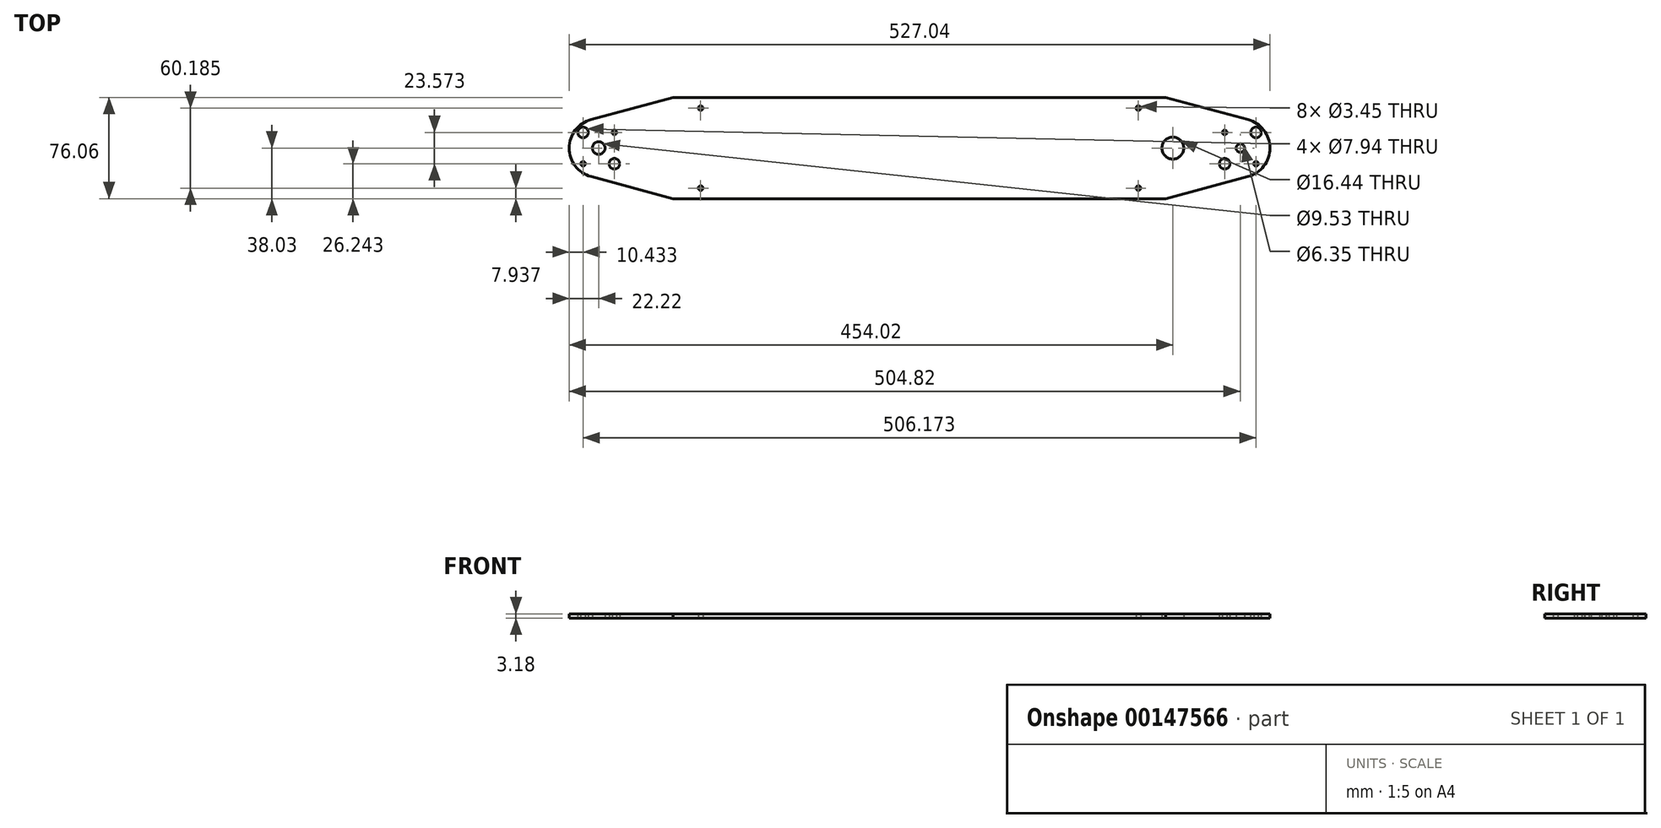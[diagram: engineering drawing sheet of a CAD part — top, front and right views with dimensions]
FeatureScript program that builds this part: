
annotation { "Feature Type Name" : "Feature", "Feature Type Description" : "" }
export const myFeature = defineFeature(function(context is Context, id is Id, definition is map)
    precondition{}
    {
        {
            var Q0;
            Q0=qCreatedBy(makeId("Top.planeOp"),FACE);
            var sketch = newSketch(context, id + "F0", { "sketchPlane" : qUnion([Q0])});
            skPoint(sketch, "E0.rect.middle", {"position": v(0, 0) * mm});
            skCircle(sketch, "E1", {"center": v(0, 0) * mm, "radius": 11.11 * mm, "construction": true});
            skLineSegment(sketch, "E2.bottom", {"start": v(11.79, 11.79) * mm, "end": v(-11.79, 11.79) * mm, "construction": true});
            skLineSegment(sketch, "E2.left", {"start": v(11.79, 11.79) * mm, "end": v(11.79, -11.79) * mm, "construction": true});
            skLineSegment(sketch, "E2.right", {"start": v(-11.79, 11.79) * mm, "end": v(-11.79, -11.79) * mm, "construction": true});
            skCircle(sketch, "E3", {"center": v(11.79, 11.79) * mm, "radius": 5.56 * mm, "construction": true});
            skCircle(sketch, "E4", {"center": v(-11.79, 11.79) * mm, "radius": 1.73 * mm});
            skCircle(sketch, "E5", {"center": v(11.79, 11.79) * mm, "radius": 3.97 * mm});
            skCircle(sketch, "E6", {"center": v(11.79, -11.79) * mm, "radius": 1.73 * mm});
            skCircle(sketch, "E7", {"center": v(-11.79, -11.79) * mm, "radius": 3.97 * mm});
            skArc(sketch, "E8", {"start": v(-488.35, 21.47) * mm, "mid": v(-504.83, 0) * mm, "end": v(-488.35, -21.47) * mm});
            skLineSegment(sketch, "E9.bottom", {"start": v(-494.39, 11.79) * mm, "end": v(-470.81, 11.79) * mm, "construction": true});
            skLineSegment(sketch, "E9.top", {"start": v(-494.39, -11.79) * mm, "end": v(-470.81, -11.79) * mm, "construction": true});
            skLineSegment(sketch, "E9.left", {"start": v(-494.39, 11.79) * mm, "end": v(-494.39, -11.79) * mm, "construction": true});
            skLineSegment(sketch, "E9.right", {"start": v(-470.81, 11.79) * mm, "end": v(-470.81, -11.79) * mm, "construction": true});
            skCircle(sketch, "E10", {"center": v(-470.81, 11.79) * mm, "radius": 1.73 * mm});
            skCircle(sketch, "E11", {"center": v(-482.6, 0) * mm, "radius": 4.76 * mm});
            skCircle(sketch, "E12", {"center": v(-494.39, 11.79) * mm, "radius": 3.97 * mm});
            skCircle(sketch, "E13", {"center": v(-494.39, -11.79) * mm, "radius": 1.73 * mm});
            skCircle(sketch, "E14", {"center": v(-470.81, -11.79) * mm, "radius": 3.97 * mm});
            skLineSegment(sketch, "E15", {"start": v(0, 0) * mm, "end": v(-482.6, 0) * mm, "construction": true});
            skLineSegment(sketch, "E16", {"start": v(-488.35, -21.47) * mm, "end": v(-426.54, -38.03) * mm});
            skLineSegment(sketch, "E17", {"start": v(-488.35, 21.47) * mm, "end": v(-426.54, 38.03) * mm});
            skLineSegment(sketch, "E18", {"start": v(-420.2, -34.86) * mm, "end": v(-62.4, -34.86) * mm, "construction": true});
            skLineSegment(sketch, "E19", {"start": v(-420.2, 34.86) * mm, "end": v(-62.4, 34.86) * mm, "construction": true});
            skLineSegment(sketch, "E20", {"start": v(-420.2, 38.03) * mm, "end": v(-420.2, 34.86) * mm, "construction": true});
            skLineSegment(sketch, "E21", {"start": v(-420.2, 38.03) * mm, "end": v(-426.54, 38.03) * mm});
            skLineSegment(sketch, "E22", {"start": v(-420.2, -34.86) * mm, "end": v(-420.2, -38.03) * mm, "construction": true});
            skLineSegment(sketch, "E23", {"start": v(-420.2, -38.03) * mm, "end": v(-426.54, -38.03) * mm});
            skLineSegment(sketch, "E24", {"start": v(-62.4, -34.86) * mm, "end": v(-62.4, -38.03) * mm, "construction": true});
            skLineSegment(sketch, "E25", {"start": v(-62.4, -38.03) * mm, "end": v(-56.06, -38.03) * mm});
            skLineSegment(sketch, "E26", {"start": v(-62.4, 34.86) * mm, "end": v(-62.4, 38.03) * mm, "construction": true});
            skLineSegment(sketch, "E27", {"start": v(-62.4, 38.03) * mm, "end": v(-56.06, 38.03) * mm});
            skLineSegment(sketch, "E28", {"start": v(-56.06, -38.03) * mm, "end": v(5.75, -21.47) * mm});
            skLineSegment(sketch, "E29", {"start": v(5.75, 21.47) * mm, "end": v(-56.06, 38.03) * mm});
            skArc(sketch, "E30", {"start": v(5.75, -21.47) * mm, "mid": v(22.23, 0) * mm, "end": v(5.75, 21.47) * mm});
            skLineSegment(sketch, "E31", {"start": v(-420.2, 34.86) * mm, "end": v(-420.2, 30.1) * mm, "construction": true});
            skLineSegment(sketch, "E32", {"start": v(-420.2, 30.1) * mm, "end": v(-405.9, 30.1) * mm, "construction": true});
            skLineSegment(sketch, "E33", {"start": v(-420.2, -34.86) * mm, "end": v(-420.2, -30.1) * mm, "construction": true});
            skLineSegment(sketch, "E34", {"start": v(-420.2, -30.1) * mm, "end": v(-405.9, -30.1) * mm, "construction": true});
            skLineSegment(sketch, "E35", {"start": v(-62.4, -34.86) * mm, "end": v(-62.4, -30.1) * mm, "construction": true});
            skLineSegment(sketch, "E36", {"start": v(-62.4, -30.1) * mm, "end": v(-76.7, -30.1) * mm, "construction": true});
            skLineSegment(sketch, "E37", {"start": v(-62.4, 34.86) * mm, "end": v(-62.4, 30.1) * mm, "construction": true});
            skLineSegment(sketch, "E38", {"start": v(-62.4, 30.1) * mm, "end": v(-76.7, 30.1) * mm, "construction": true});
            skCircle(sketch, "E39", {"center": v(-405.9, 30.1) * mm, "radius": 1.73 * mm});
            skCircle(sketch, "E40", {"center": v(-76.7, 30.1) * mm, "radius": 1.73 * mm});
            skCircle(sketch, "E41", {"center": v(-76.7, -30.1) * mm, "radius": 1.73 * mm});
            skCircle(sketch, "E42", {"center": v(-405.9, -30.1) * mm, "radius": 1.73 * mm});
            skLineSegment(sketch, "E43", {"start": v(-11.79, -11.79) * mm, "end": v(11.79, -11.79) * mm, "construction": true});
            skLineSegment(sketch, "E44", {"start": v(-241.3, -34.86) * mm, "end": v(-241.3, 0) * mm, "construction": true});
            skLineSegment(sketch, "E45", {"start": v(-241.3, 0) * mm, "end": v(-241.3, 34.86) * mm, "construction": true});
            skCircle(sketch, "E46", {"center": v(-50.8, 0) * mm, "radius": 8.22 * mm});
            skCircle(sketch, "E47", {"center": v(0, 0) * mm, "radius": 3.18 * mm});
            skCircle(sketch, "E48", {"center": v(-494.39, 11.79) * mm, "radius": 5.56 * mm, "construction": true});
            skLineSegment(sketch, "E49", {"start": v(5.75, 21.47) * mm, "end": v(-25.15, 21.47) * mm, "construction": true});
            skLineSegment(sketch, "E50", {"start": v(-25.15, 21.47) * mm, "end": v(-25.15, 29.75) * mm, "construction": true});
            skLineSegment(sketch, "E51", {"start": v(-488.35, 21.47) * mm, "end": v(-457.45, 21.47) * mm, "construction": true});
            skLineSegment(sketch, "E52", {"start": v(-457.45, 21.47) * mm, "end": v(-457.45, 29.75) * mm, "construction": true});
            skCircle(sketch, "E53", {"center": v(-482.6, 0) * mm, "radius": 63.67 * mm, "construction": true});
            skLineSegment(sketch, "E54", {"start": v(-420.2, 38.03) * mm, "end": v(-62.4, 38.03) * mm});
            skLineSegment(sketch, "E55", {"start": v(-62.4, -38.03) * mm, "end": v(-420.2, -38.03) * mm});
            skSolve(sketch);
        }
        {
            var Q0;
            Q0=qSketchRegion(id+"F0",true);
            extrude(context, id + "F1", {"entities" : qUnion([Q0]), "depth" : 3.17 * mm});
        }
    });
